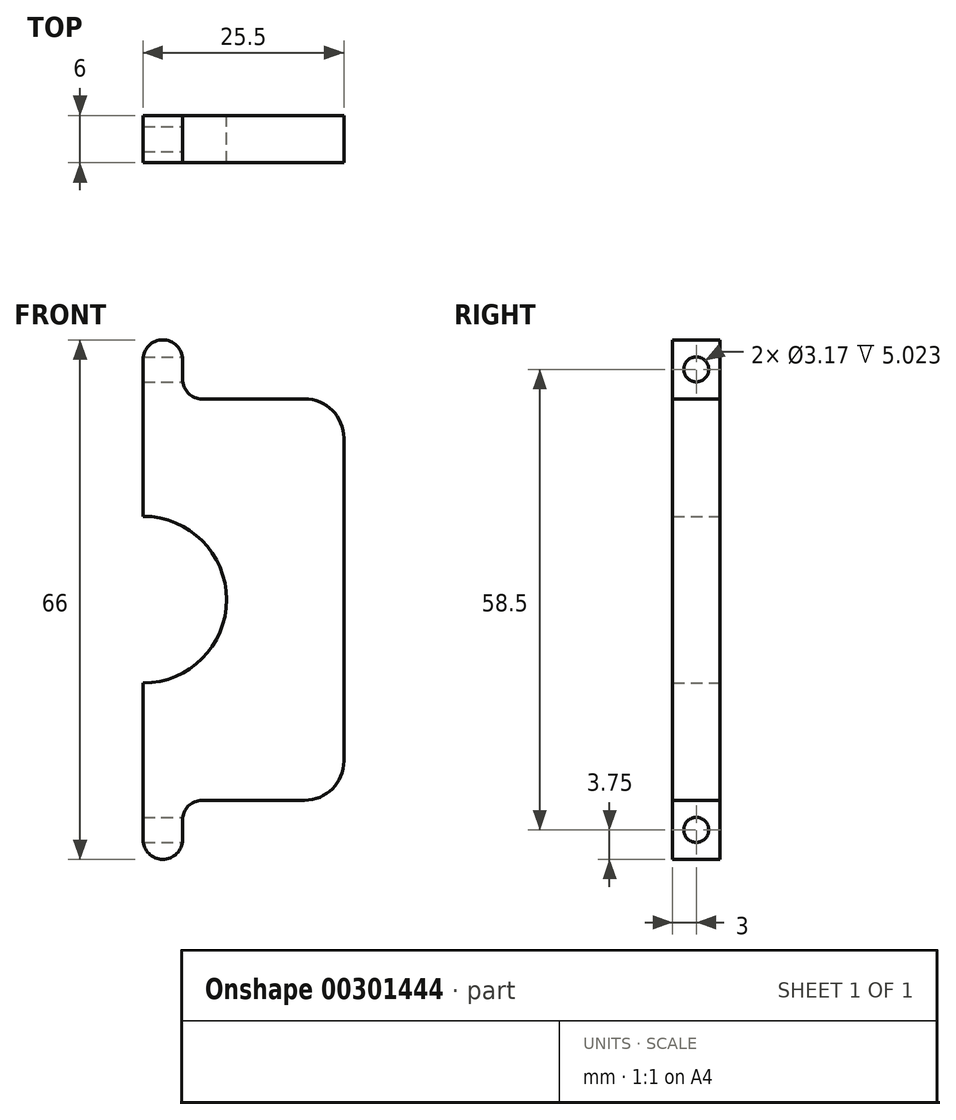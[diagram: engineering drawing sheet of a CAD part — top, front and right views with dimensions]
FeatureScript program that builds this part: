
annotation { "Feature Type Name" : "Feature", "Feature Type Description" : "" }
export const myFeature = defineFeature(function(context is Context, id is Id, definition is map)
    precondition{}
    {
        {
            var Q0;
            Q0=qCreatedBy(makeId("Front.planeOp"),FACE);
            var sketch = newSketch(context, id + "F0", { "sketchPlane" : qUnion([Q0])});
            skLineSegment(sketch, "E0", {"start": v(12.75, 0) * mm, "end": v(12.75, 20.5) * mm});
            skLineSegment(sketch, "E1", {"start": v(-12.75, 25.5) * mm, "end": v(-12.75, 10.6) * mm});
            skLineSegment(sketch, "E2", {"start": v(-12.75, -25.5) * mm, "end": v(-12.75, -10.6) * mm});
            skArc(sketch, "E3", {"start": v(-12.75, -10.6) * mm, "mid": v(-2.16, 0) * mm, "end": v(-12.75, 10.6) * mm});
            skLineSegment(sketch, "E4.bottom", {"start": v(-12.75, 25.5) * mm, "end": v(-7.75, 25.5) * mm});
            skLineSegment(sketch, "E5.bottom", {"start": v(-12.75, -25.5) * mm, "end": v(-7.75, -25.5) * mm});
            skLineSegment(sketch, "E5.left", {"start": v(-12.75, -25.5) * mm, "end": v(-12.75, -30.5) * mm});
            skLineSegment(sketch, "E5.right", {"start": v(-7.75, -28) * mm, "end": v(-7.75, -30.5) * mm});
            skLineSegment(sketch, "E6", {"start": v(-12.75, 30.5) * mm, "end": v(-12.75, 29.25) * mm});
            skLineSegment(sketch, "E7", {"start": v(-7.75, 30.5) * mm, "end": v(-7.75, 29.25) * mm});
            skLineSegment(sketch, "E8", {"start": v(-12.75, -25.5) * mm, "end": v(-12.75, -29.25) * mm});
            skLineSegment(sketch, "E9", {"start": v(-7.75, -25.5) * mm, "end": v(-7.75, -29.25) * mm});
            skLineSegment(sketch, "E10", {"start": v(-5.25, 25.5) * mm, "end": v(-5.25, 25.5) * mm});
            skLineSegment(sketch, "E11", {"start": v(-5.25, -25.5) * mm, "end": v(-5.25, -25.5) * mm});
            skPoint(sketch, "E12.visualSharp", {"position": v(-7.75, 25.5) * mm});
            skArc(sketch, "E12.filletArc", {"start": v(-7.75, 28) * mm, "mid": v(-7.02, 26.23) * mm, "end": v(-5.25, 25.5) * mm});
            skPoint(sketch, "E13.visualSharp", {"position": v(-7.75, -25.5) * mm});
            skArc(sketch, "E13.filletArc", {"start": v(-5.25, -25.5) * mm, "mid": v(-7.02, -26.23) * mm, "end": v(-7.75, -28) * mm});
            skLineSegment(sketch, "E14", {"start": v(-10.25, -33) * mm, "end": v(-10.25, -33) * mm});
            skPoint(sketch, "E15.visualSharp", {"position": v(-7.75, -33) * mm});
            skArc(sketch, "E15.filletArc", {"start": v(-10.25, -33) * mm, "mid": v(-8.48, -32.27) * mm, "end": v(-7.75, -30.5) * mm});
            skPoint(sketch, "E16.visualSharp", {"position": v(-12.75, -33) * mm});
            skArc(sketch, "E16.filletArc", {"start": v(-12.75, -30.5) * mm, "mid": v(-12.02, -32.27) * mm, "end": v(-10.25, -33) * mm});
            skLineSegment(sketch, "E17", {"start": v(12.75, -20.5) * mm, "end": v(12.75, -20.5) * mm});
            skLineSegment(sketch, "E18", {"start": v(7.75, -25.5) * mm, "end": v(7.75, -25.5) * mm});
            skPoint(sketch, "E19.visualSharp", {"position": v(12.75, -25.5) * mm});
            skArc(sketch, "E19.filletArc", {"start": v(7.75, -25.5) * mm, "mid": v(11.29, -24.04) * mm, "end": v(12.75, -20.5) * mm});
            skLineSegment(sketch, "E20", {"start": v(7.75, 25.5) * mm, "end": v(7.75, 25.5) * mm});
            skPoint(sketch, "E21.visualSharp", {"position": v(12.75, 25.5) * mm});
            skArc(sketch, "E21.filletArc", {"start": v(12.75, 20.5) * mm, "mid": v(11.29, 24.04) * mm, "end": v(7.75, 25.5) * mm});
            skLineSegment(sketch, "E22", {"start": v(-5.25, 25.5) * mm, "end": v(7.75, 25.5) * mm});
            skLineSegment(sketch, "E23", {"start": v(-5.25, -25.5) * mm, "end": v(7.75, -25.5) * mm});
            skLineSegment(sketch, "E24", {"start": v(12.75, 0) * mm, "end": v(12.75, -20.5) * mm});
            skLineSegment(sketch, "E25", {"start": v(-10.25, 33) * mm, "end": v(-10.25, 33) * mm});
            skPoint(sketch, "E26.visualSharp", {"position": v(-7.75, 33) * mm});
            skArc(sketch, "E26.filletArc", {"start": v(-7.75, 30.5) * mm, "mid": v(-8.48, 32.27) * mm, "end": v(-10.25, 33) * mm});
            skPoint(sketch, "E27.visualSharp", {"position": v(-12.75, 33) * mm});
            skArc(sketch, "E27.filletArc", {"start": v(-10.25, 33) * mm, "mid": v(-12.02, 32.27) * mm, "end": v(-12.75, 30.5) * mm});
            skLineSegment(sketch, "E28", {"start": v(-12.75, 29.25) * mm, "end": v(-12.75, 25.5) * mm});
            skLineSegment(sketch, "E29", {"start": v(-7.75, 29.25) * mm, "end": v(-7.75, 28) * mm});
            skSolve(sketch);
        }
        {
            var Q0;
            Q0=makeQuery(id+"F0.imprint","IMPRINT",FACE,{"disambiguationData":[TD([[makeQuery(id+"F0.imprint","IMPRINT",EDGE,{"derivedFrom":sQuery(id+"F0.wireOp",EDGE,"E0")}),1.0]])]});
            var Q1;
            Q1=makeQuery(id+"F0.imprint","IMPRINT",FACE,{"disambiguationData":[TD([[makeQuery(id+"F0.imprint","IMPRINT",EDGE,{"derivedFrom":sQuery(id+"F0.wireOp",EDGE,"E4.bottom")}),1.0]])]});
            var Q2;
            Q2=makeQuery(id+"F0.imprint","IMPRINT",FACE,{"disambiguationData":[TD([[makeQuery(id+"F0.imprint","IMPRINT",EDGE,{"derivedFrom":sQuery(id+"F0.wireOp",EDGE,"E5.bottom")}),-1.0]])]});
            extrude(context, id + "F1", {"entities" : qUnion([Q0, Q1, Q2]), "endBound" : BoundingType.SYMMETRIC, "depth" : 6 * mm});
        }
        {
            var Q0;
            Q0=qCreatedBy(makeId("Right.planeOp"),FACE);
            var sketch = newSketch(context, id + "F2", { "sketchPlane" : qUnion([Q0])});
            skCircle(sketch, "E30", {"center": v(0, 29.25) * mm, "radius": 1.59 * mm});
            skCircle(sketch, "E31", {"center": v(0, -29.25) * mm, "radius": 1.59 * mm});
            skSolve(sketch);
        }
        {
            var Q0;
            Q0=makeQuery(id+"F2.imprint","IMPRINT",FACE,{"disambiguationData":[TD([[makeQuery(id+"F2.imprint","IMPRINT",EDGE,{"derivedFrom":sQuery(id+"F2.wireOp",EDGE,"E30")}),1.0]])]});
            var Q1;
            Q1=makeQuery(id+"F2.imprint","IMPRINT",FACE,{"disambiguationData":[TD([[makeQuery(id+"F2.imprint","IMPRINT",EDGE,{"derivedFrom":sQuery(id+"F2.wireOp",EDGE,"E31")}),1.0]])]});
            extrude(context, id + "F3", {"entities" : qUnion([Q0, Q1]), "operationType" : NewBodyOperationType.REMOVE, "endBound" : BoundingType.THROUGH_ALL, "oppositeDirection" : true, "depth" : 25 * mm});
        }
    });
